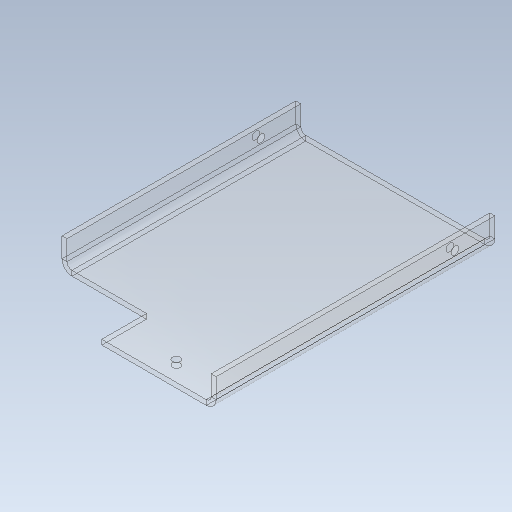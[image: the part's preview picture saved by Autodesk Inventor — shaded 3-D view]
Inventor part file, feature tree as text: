
AUTODESK INVENTOR PART (.ipt)
format: ipt  version: 2020 (Build 240168000, 168)  size: 205,312 bytes
history: native  units: in
note: dims shown in document units (in); Inventor stores cm internally (conversion verified against a paired STEP export)
features: sketch x6, sheet_metal_op x4, other x4, hole x3, projected_geometry x1
ambient origin geometry x8: Origin, YZ Plane, XZ Plane, XY Plane, X Axis, Y Axis, Z Axis, Center Point
bodies: Solid1 (feature_tree)
feature tree (18):
  sheet_metal_op  "Face1"
  sheet_metal_op  "Flange1"
  hole  "Hole1"  [1 undecoded]
  hole  "Hole2"  [1 undecoded]
  hole  "Hole3"  [1 undecoded]
  sketch  "Sketch1"  dims[d0=7.0in d1=5.0in]
  other  "Plate1"
  sketch  "Sketch2"  dims[d2=0.125in d3=1.125in]
  sketch  "Sketch3"  dims[d4=2.125in d5=0.125in]
  other  "Plate2"
  sheet_metal_op  "Bend1"
  sheet_metal_op  "Corner1"
  sketch  "Sketch4"  dims[d6=0.0in]
  sketch  "Sketch5"  dims[d7=0.125in]
  sketch  "Sketch6"  dims[d8=0.0625in d9=0.25in d10=0.125in d11=0.75in d12=90.0deg d13=0.125in d14=0.5in d15=0.125in d16=0.125in d17=0.196in d18=0.75in d19=0.375in d20=0.25in d21=0.5635in d22=0.125in d23=0.8108in d24=1.5in d25=0.5in d26=0.196in d27=0.75in d28=0.375in d29=0.25in d30=0.5635in d31=0.125in d32=0.8108in d33=0.25in d34=1.0in d35=0.196in d36=0.75in d37=0.375in d38=0.25in d39=0.5635in d40=0.125in d41=0.8108in d42=0.25in d43=1.0in]
  other  "Cut1"
  other  "Definition1"
  projected_geometry  "Projected Loop1"
note: 3 required parameter values undecoded (feature->parameter linkage not recoverable at this tier; creation-order binding heuristic only, values carry confidence <= 0.55)
